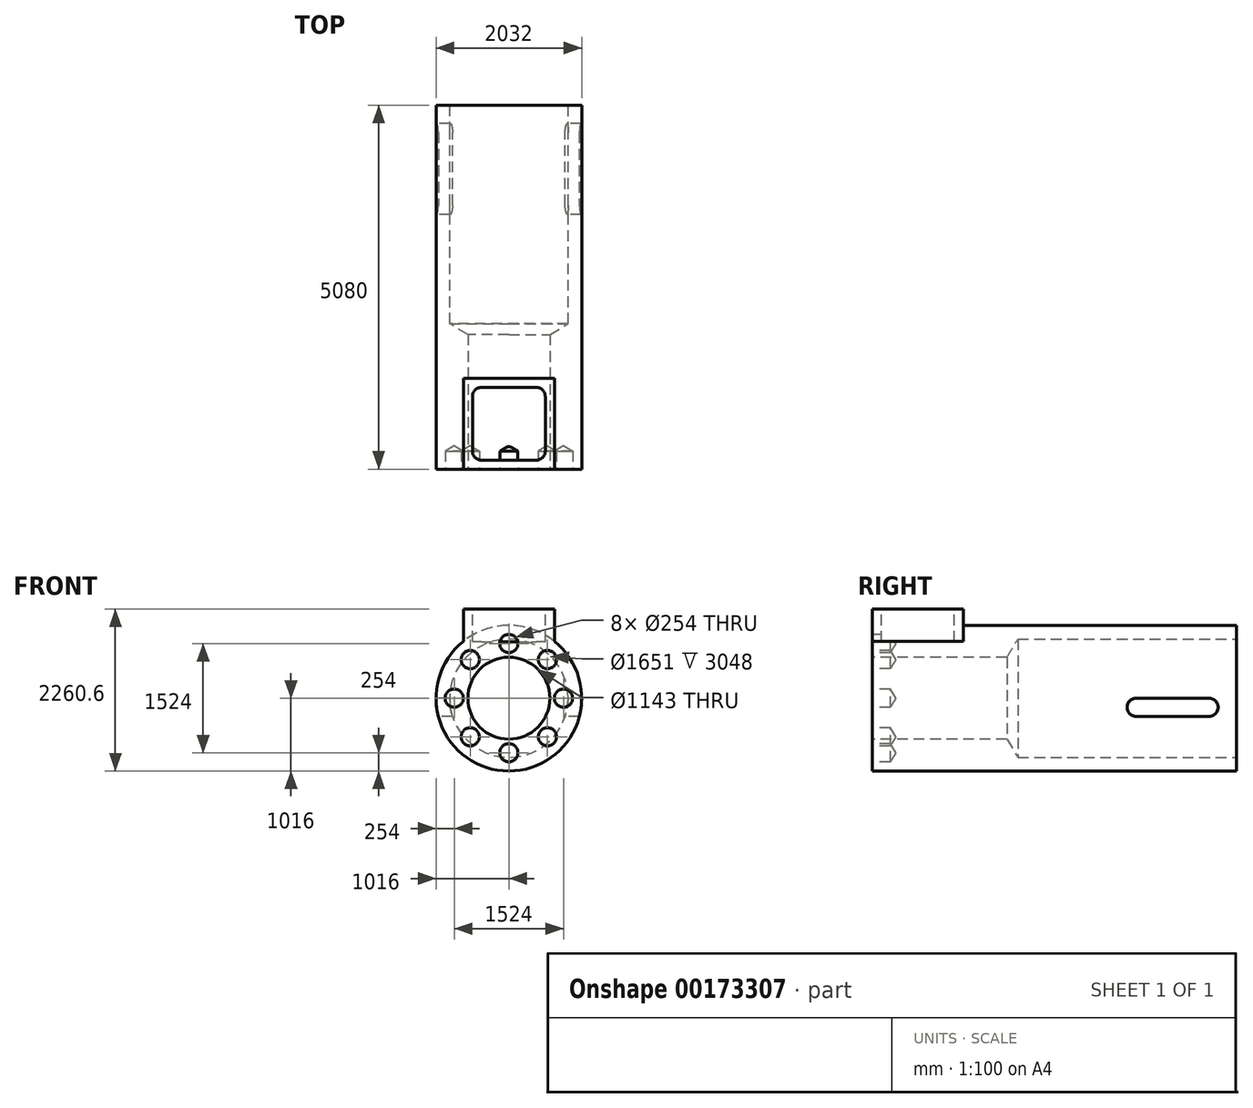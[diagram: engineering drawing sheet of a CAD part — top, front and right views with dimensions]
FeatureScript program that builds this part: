
annotation { "Feature Type Name" : "Feature", "Feature Type Description" : "" }
export const myFeature = defineFeature(function(context is Context, id is Id, definition is map)
    precondition{}
    {
        {
            var Q0;
            Q0=qCreatedBy(makeId("Front.planeOp"),FACE);
            var sketch = newSketch(context, id + "F0", { "sketchPlane" : qUnion([Q0])});
            skCircle(sketch, "E0", {"center": v(0, 0) * mm, "radius": 1016 * mm});
            skLineSegment(sketch, "E1", {"start": v(0, 787.4) * mm, "end": v(635, 787.4) * mm});
            skLineSegment(sketch, "E2", {"start": v(0, 787.4) * mm, "end": v(-635, 787.4) * mm});
            skLineSegment(sketch, "E3", {"start": v(-635, 787.4) * mm, "end": v(-635, 1244.6) * mm});
            skLineSegment(sketch, "E4", {"start": v(635, 787.4) * mm, "end": v(635, 1244.6) * mm});
            skLineSegment(sketch, "E5", {"start": v(-635, 1244.6) * mm, "end": v(635, 1244.6) * mm});
            skLineSegment(sketch, "E6", {"start": v(0, 1016) * mm, "end": v(-635, 1016) * mm});
            skLineSegment(sketch, "E7", {"start": v(0, 1016) * mm, "end": v(635, 1016) * mm});
            skCircle(sketch, "E8", {"center": v(0, 762) * mm, "radius": 127 * mm});
            skCircle(sketch, "E9.1.0", {"center": v(-538.82, 538.82) * mm, "radius": 127 * mm});
            skCircle(sketch, "E9.2.0", {"center": v(-762, 0) * mm, "radius": 127 * mm});
            skCircle(sketch, "E9.3.0", {"center": v(-538.82, -538.82) * mm, "radius": 127 * mm});
            skCircle(sketch, "E9.4.0", {"center": v(0, -762) * mm, "radius": 127 * mm});
            skCircle(sketch, "E9.5.0", {"center": v(538.82, -538.82) * mm, "radius": 127 * mm});
            skCircle(sketch, "E9.6.0", {"center": v(762, 0) * mm, "radius": 127 * mm});
            skCircle(sketch, "E9.7.0", {"center": v(538.82, 538.82) * mm, "radius": 127 * mm});
            skSolve(sketch);
        }
        {
            var Q0;
            Q0=makeQuery(id+"F0.imprint","IMPRINT",FACE,{"disambiguationData":[TD([[makeQuery(id+"F0.imprint","IMPRINT",EDGE,{"derivedFrom":sQuery(id+"F0.wireOp",EDGE,"E9.1.0")}),-1.0]])]});
            var Q1;
            {var subQ5=sQuery(id+"F0.wireOp",EDGE,"E4");var subQ6=sQuery(id+"F0.wireOp",EDGE,"E1");var subQ7=makeQuery(id+"F0.imprint","INTERSECT",VERTEX,{"derivedFrom":[subQ6,subQ5]});Q1=makeQuery(id+"F0.imprint","IMPRINT",FACE,{"disambiguationData":[TD([[makeQuery(id+"F0.imprint","IMPRINT",EDGE,{"disambiguationData":[TD([[subQ7,1.0]])],"derivedFrom":subQ6}),1.0]])]});}
            var Q2;
            Q2=makeQuery(id+"F0.imprint","IMPRINT",FACE,{"disambiguationData":[TD([[makeQuery(id+"F0.imprint","IMPRINT",EDGE,{"derivedFrom":sQuery(id+"F0.wireOp",EDGE,"E9.7.0")}),1.0]])]});
            var Q3;
            {var subQ0=sQuery(id+"F0.wireOp",EDGE,"E2");var subQ1=sQuery(id+"F0.wireOp",EDGE,"E1");var subQ2=makeQuery(id+"F0.imprint","INTERSECT",VERTEX,{"derivedFrom":[subQ1,subQ0]});Q3=makeQuery(id+"F0.imprint","IMPRINT",FACE,{"disambiguationData":[TD([[makeQuery(id+"F0.imprint","IMPRINT",EDGE,{"disambiguationData":[TD([[subQ2,-1.0]])],"derivedFrom":subQ1}),-1.0]])]});}
            var Q4;
            Q4=makeQuery(id+"F0.imprint","IMPRINT",FACE,{"disambiguationData":[TD([[makeQuery(id+"F0.imprint","IMPRINT",EDGE,{"derivedFrom":sQuery(id+"F0.wireOp",EDGE,"E9.1.0")}),1.0]])]});
            var Q5;
            Q5=makeQuery(id+"F0.imprint","IMPRINT",FACE,{"disambiguationData":[TD([[makeQuery(id+"F0.imprint","IMPRINT",EDGE,{"derivedFrom":sQuery(id+"F0.wireOp",EDGE,"E9.2.0")}),1.0]])]});
            var Q6;
            Q6=makeQuery(id+"F0.imprint","IMPRINT",FACE,{"disambiguationData":[TD([[makeQuery(id+"F0.imprint","IMPRINT",EDGE,{"derivedFrom":sQuery(id+"F0.wireOp",EDGE,"E9.3.0")}),1.0]])]});
            var Q7;
            Q7=makeQuery(id+"F0.imprint","IMPRINT",FACE,{"disambiguationData":[TD([[makeQuery(id+"F0.imprint","IMPRINT",EDGE,{"derivedFrom":sQuery(id+"F0.wireOp",EDGE,"E9.4.0")}),1.0]])]});
            var Q8;
            Q8=makeQuery(id+"F0.imprint","IMPRINT",FACE,{"disambiguationData":[TD([[makeQuery(id+"F0.imprint","IMPRINT",EDGE,{"derivedFrom":sQuery(id+"F0.wireOp",EDGE,"E9.5.0")}),1.0]])]});
            var Q9;
            Q9=makeQuery(id+"F0.imprint","IMPRINT",FACE,{"disambiguationData":[TD([[makeQuery(id+"F0.imprint","IMPRINT",EDGE,{"derivedFrom":sQuery(id+"F0.wireOp",EDGE,"E9.6.0")}),1.0]])]});
            var Q10;
            {var subQ0=sQuery(id+"F0.wireOp",EDGE,"E2");var subQ1=sQuery(id+"F0.wireOp",EDGE,"E1");var subQ2=makeQuery(id+"F0.imprint","INTERSECT",VERTEX,{"derivedFrom":[subQ1,subQ0]});Q10=makeQuery(id+"F0.imprint","IMPRINT",FACE,{"disambiguationData":[TD([[makeQuery(id+"F0.imprint","IMPRINT",EDGE,{"disambiguationData":[TD([[subQ2,-1.0]])],"derivedFrom":subQ1}),1.0]])]});}
            extrude(context, id + "F1", {"entities" : qUnion([Q0, Q1, Q2, Q3, Q4, Q5, Q6, Q7, Q8, Q9, Q10]), "oppositeDirection" : true, "depth" : 5080 * mm});
        }
        {
            var Q0;
            {var subQ1=sQuery(id+"F0.wireOp",EDGE,"E5");Q0=makeQuery(id+"F0.imprint","IMPRINT",FACE,{"disambiguationData":[TD([[makeQuery(id+"F0.imprint","IMPRINT",EDGE,{"derivedFrom":subQ1}),-1.0]])]});}
            var Q1;
            {var subQ0=sQuery(id+"F0.wireOp",EDGE,"E7");Q1=makeQuery(id+"F0.imprint","IMPRINT",FACE,{"disambiguationData":[TD([[makeQuery(id+"F0.imprint","IMPRINT",EDGE,{"derivedFrom":subQ0}),-1.0]])]});}
            var Q2;
            {var subQ0=sQuery(id+"F0.wireOp",EDGE,"E6");Q2=makeQuery(id+"F0.imprint","IMPRINT",FACE,{"disambiguationData":[TD([[makeQuery(id+"F0.imprint","IMPRINT",EDGE,{"derivedFrom":subQ0}),1.0]])]});}
            extrude(context, id + "F2", {"entities" : qUnion([Q0, Q1, Q2]), "operationType" : NewBodyOperationType.ADD, "oppositeDirection" : true, "depth" : 1270 * mm});
        }
        {
            var Q0;
            Q0=makeQuery(id+"F2.opExtrude","SWEPT_FACE",FACE,{"disambiguationData":[OSD([sQuery(id+"F0.wireOp",EDGE,"E5")])]});
            var sketch = newSketch(context, id + "F3", { "sketchPlane" : qUnion([Q0])});
            skLineSegment(sketch, "E10", {"start": v(0, 0) * mm, "end": v(0, -127) * mm});
            skPoint(sketch, "E10.endSnap0", {"position": v(0, 0) * mm});
            skLineSegment(sketch, "E11", {"start": v(-635, 635) * mm, "end": v(-508, 635) * mm});
            skLineSegment(sketch, "E12", {"start": v(0, 1270) * mm, "end": v(0, 1397) * mm});
            skLineSegment(sketch, "E13", {"start": v(635, 635) * mm, "end": v(508, 635) * mm});
            skPoint(sketch, "E13.endSnap0", {"position": v(635, 635) * mm});
            skLineSegment(sketch, "E14.bottom", {"start": v(-508, 1143) * mm, "end": v(508, 1143) * mm});
            skLineSegment(sketch, "E14.top", {"start": v(-508, 127) * mm, "end": v(508, 127) * mm});
            skLineSegment(sketch, "E14.left", {"start": v(-508, 1143) * mm, "end": v(-508, 127) * mm});
            skLineSegment(sketch, "E14.right", {"start": v(508, 1143) * mm, "end": v(508, 127) * mm});
            skPoint(sketch, "E14.middle", {"position": v(0, 635) * mm});
            skSolve(sketch);
        }
        {
            var Q0;
            {var subQ6=sQuery(id+"F3.wireOp",EDGE,"E14.bottom");var subQ7=makeQuery(id+"F3.imprint","INTERSECT",VERTEX,{"derivedFrom":[sQuery(id+"F3.wireOp",EDGE,"E10"),subQ6]});Q0=makeQuery(id+"F3.imprint","IMPRINT",FACE,{"disambiguationData":[TD([[makeQuery(id+"F3.imprint","IMPRINT",EDGE,{"disambiguationData":[TD([[subQ7,1.0]])],"derivedFrom":subQ6}),-1.0]])]});}
            extrude(context, id + "F4", {"entities" : qUnion([Q0]), "operationType" : NewBodyOperationType.REMOVE, "oppositeDirection" : true, "depth" : 457.2 * mm});
        }
        {
            var Q0;
            Q0=sQuery(id+"F0.wireOp",VERTEX,"E0.center");
            var Q1;
            Q1=makeQuery(id+"F1.opExtrude","SWEPT_BODY",BODY,{"disambiguationData":[OSD([sQuery(id+"F0.wireOp",EDGE,"E0")])]});
            hole(context, id + "F5", {"style" : HoleStyle.SIMPLE, "endStyle" : HoleEndStyle.THROUGH, "holeDiameter" : 1143 * mm, "locations" : qUnion([Q0]), "scope" : qUnion([Q1]), "isTappedThrough" : true});
        }
        {
            var Q0;
            Q0=makeQuery(id+"F1.opExtrude","CAP_FACE",FACE,{"disambiguationData":[OSD([sQuery(id+"F0.wireOp",EDGE,"E0")])],"isStart":false});
            var sketch = newSketch(context, id + "F6", { "sketchPlane" : qUnion([Q0])});
            skLineSegment(sketch, "E15", {"start": v(0, 571.5) * mm, "end": v(0, -571.5) * mm});
            skLineSegment(sketch, "E16", {"start": v(0, 0) * mm, "end": v(571.5, 0) * mm});
            skLineSegment(sketch, "E17", {"start": v(0, 0) * mm, "end": v(-571.5, 0) * mm});
            skSolve(sketch);
        }
        {
            var Q0;
            Q0=sQuery(id+"F6.wireOp",VERTEX,"E16.start");
            var Q1;
            Q1=makeQuery(id+"F1.opExtrude","SWEPT_BODY",BODY,{"disambiguationData":[OSD([sQuery(id+"F0.wireOp",EDGE,"E0")])]});
            hole(context, id + "F7", {"style" : HoleStyle.SIMPLE, "endStyle" : HoleEndStyle.BLIND, "holeDiameter" : 1651 * mm, "holeDepth" : 3048 * mm, "locations" : qUnion([Q0]), "scope" : qUnion([Q1])});
        }
        {
            var Q0;
            Q0=sQuery(id+"F0.wireOp",VERTEX,"E8.center");
            var Q1;
            Q1=sQuery(id+"F0.wireOp",VERTEX,"E9.7.0.center");
            var Q2;
            Q2=sQuery(id+"F0.wireOp",VERTEX,"E9.6.0.center");
            var Q3;
            Q3=sQuery(id+"F0.wireOp",VERTEX,"E9.5.0.center");
            var Q4;
            Q4=sQuery(id+"F0.wireOp",VERTEX,"E9.4.0.center");
            var Q5;
            Q5=sQuery(id+"F0.wireOp",VERTEX,"E9.3.0.center");
            var Q6;
            Q6=sQuery(id+"F0.wireOp",VERTEX,"E9.2.0.center");
            var Q7;
            Q7=sQuery(id+"F0.wireOp",VERTEX,"E9.1.0.center");
            var Q8;
            Q8=makeQuery(id+"F1.opExtrude","SWEPT_BODY",BODY,{"disambiguationData":[OSD([sQuery(id+"F0.wireOp",EDGE,"E0")])]});
            hole(context, id + "F8", {"style" : HoleStyle.SIMPLE, "endStyle" : HoleEndStyle.BLIND, "holeDiameter" : 254 * mm, "holeDepth" : 254 * mm, "locations" : qUnion([Q0, Q1, Q2, Q3, Q4, Q5, Q6, Q7]), "scope" : qUnion([Q8])});
        }
        {
            var Q0;
            Q0=qCreatedBy(makeId("Right.planeOp"),FACE);
            var sketch = newSketch(context, id + "F9", { "sketchPlane" : qUnion([Q0])});
            skLineSegment(sketch, "E18", {"start": v(3683, 0) * mm, "end": v(4699, 0) * mm});
            skLineSegment(sketch, "E19", {"start": v(3683, -254) * mm, "end": v(4699, -254) * mm});
            skLineSegment(sketch, "E20", {"start": v(4699, 0) * mm, "end": v(4699, -254) * mm});
            skLineSegment(sketch, "E21", {"start": v(3683, -254) * mm, "end": v(3683, 0) * mm});
            skArc(sketch, "E22", {"start": v(4699, -254) * mm, "mid": v(4826, -127) * mm, "end": v(4699, 0) * mm});
            skArc(sketch, "E23", {"start": v(3683, 0) * mm, "mid": v(3556, -127) * mm, "end": v(3683, -254) * mm});
            skSolve(sketch);
        }
        {
            var Q0;
            Q0 = qSketchRegion(id + "F9", true);
            extrude(context, id + "F10", {"entities" : qUnion([Q0]), "operationType" : NewBodyOperationType.REMOVE, "endBound" : BoundingType.SYMMETRIC, "depth" : 2032 * mm});
        }
        {
            var Q0;
            Q0=makeQuery(id+"F4.boolean.opBoolean","COPY",EDGE,{"derivedFrom":makeQuery(id+"F4.opExtrude","SWEPT_EDGE",EDGE,{"disambiguationData":[OSD([sQuery(id+"F3.wireOp",EDGE,"E14.top"),sQuery(id+"F3.wireOp",EDGE,"E14.left")])]})});
            var Q1;
            Q1=makeQuery(id+"F4.boolean.opBoolean","COPY",EDGE,{"derivedFrom":makeQuery(id+"F4.opExtrude","SWEPT_EDGE",EDGE,{"disambiguationData":[OSD([sQuery(id+"F3.wireOp",EDGE,"E14.bottom"),sQuery(id+"F3.wireOp",EDGE,"E14.left")])]})});
            var Q2;
            Q2=makeQuery(id+"F4.boolean.opBoolean","COPY",EDGE,{"derivedFrom":makeQuery(id+"F4.opExtrude","SWEPT_EDGE",EDGE,{"disambiguationData":[OSD([sQuery(id+"F3.wireOp",EDGE,"E14.top"),sQuery(id+"F3.wireOp",EDGE,"E14.right")])]})});
            var Q3;
            Q3=makeQuery(id+"F4.boolean.opBoolean","COPY",EDGE,{"derivedFrom":makeQuery(id+"F4.opExtrude","SWEPT_EDGE",EDGE,{"disambiguationData":[OSD([sQuery(id+"F3.wireOp",EDGE,"E14.bottom"),sQuery(id+"F3.wireOp",EDGE,"E14.right")])]})});
            fillet(context, id + "F11", {"entities" : qUnion([Q0, Q1, Q2, Q3]), "radius" : 127 * mm, "tangentPropagation" : true, "allowEdgeOverflow" : false});
        }
    });
